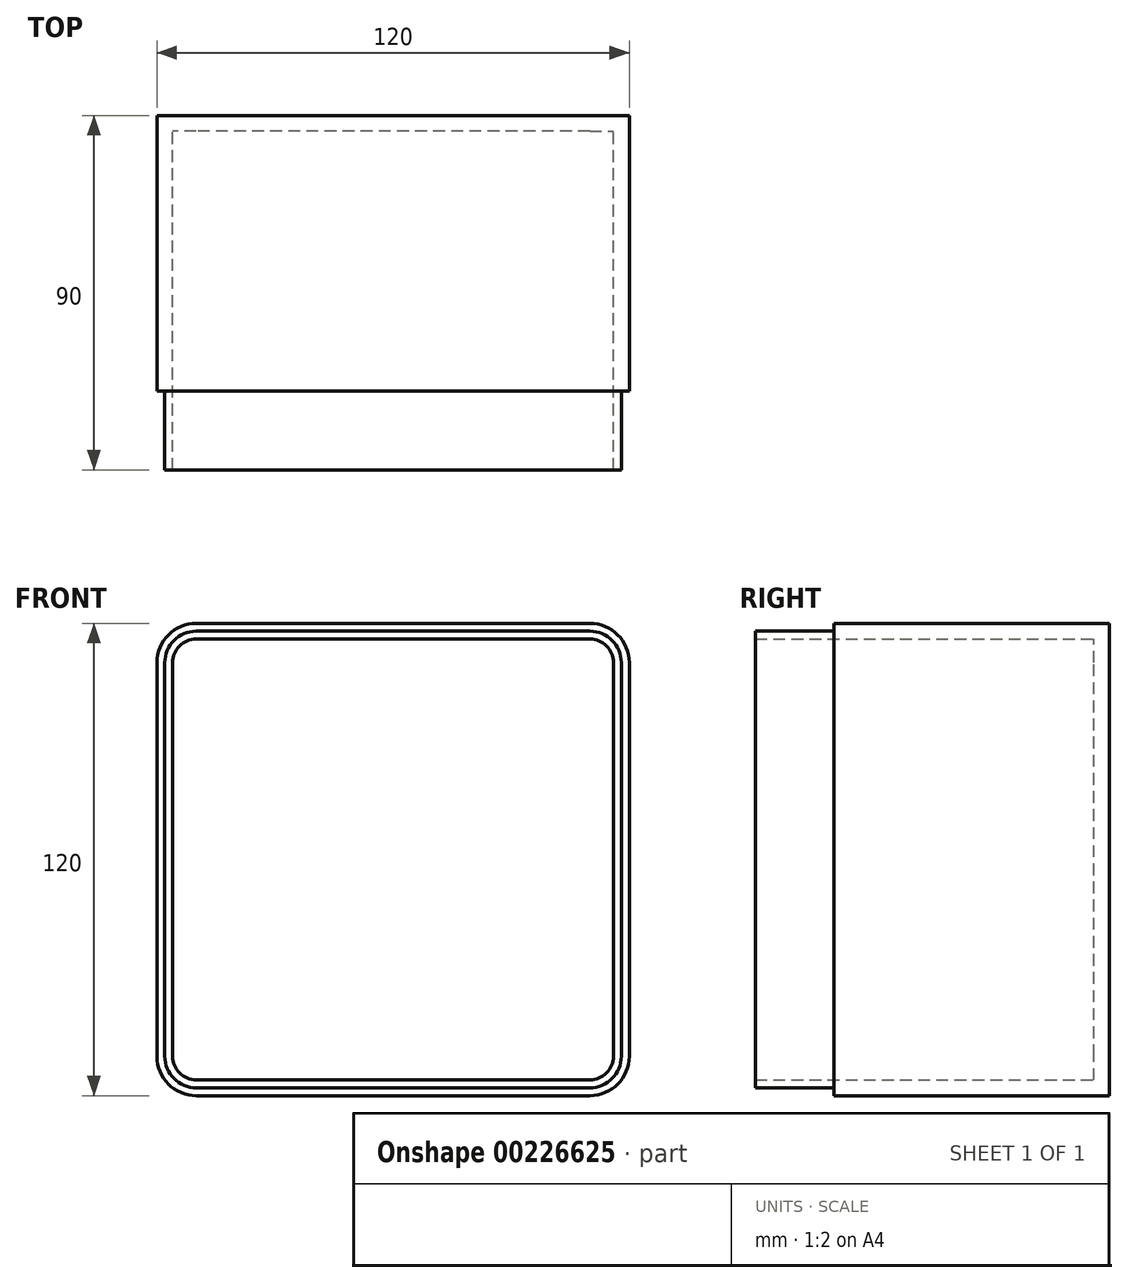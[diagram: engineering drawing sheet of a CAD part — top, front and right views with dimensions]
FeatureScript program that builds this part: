
annotation { "Feature Type Name" : "Feature", "Feature Type Description" : "" }
export const myFeature = defineFeature(function(context is Context, id is Id, definition is map)
    precondition{}
    {
        {
            var Q0;
            Q0=qCreatedBy(makeId("Front.planeOp"),FACE);
            var sketch = newSketch(context, id + "F0", { "sketchPlane" : qUnion([Q0])});
            skLineSegment(sketch, "E0.bottom", {"start": v(0, 0) * mm, "end": v(-120, 0) * mm});
            skLineSegment(sketch, "E0.top", {"start": v(0, 120) * mm, "end": v(-120, 120) * mm});
            skLineSegment(sketch, "E0.left", {"start": v(0, 0) * mm, "end": v(0, 120) * mm});
            skLineSegment(sketch, "E0.right", {"start": v(-120, 0) * mm, "end": v(-120, 120) * mm});
            skSolve(sketch);
        }
        {
            var Q0;
            Q0 = qSketchRegion(id + "F0", true);
            extrude(context, id + "F1", {"entities" : qUnion([Q0]), "depth" : 90 * mm});
        }
        {
            var Q0;
            Q0=makeQuery(id+"F1.opExtrude","SWEPT_EDGE",EDGE,{"disambiguationData":[OSD([sQuery(id+"F0.wireOp",EDGE,"E0.top"),sQuery(id+"F0.wireOp",EDGE,"E0.left")])]});
            var Q1;
            Q1=makeQuery(id+"F1.opExtrude","SWEPT_EDGE",EDGE,{"disambiguationData":[OSD([sQuery(id+"F0.wireOp",EDGE,"E0.top"),sQuery(id+"F0.wireOp",EDGE,"E0.right")])]});
            var Q2;
            Q2=makeQuery(id+"F1.opExtrude","SWEPT_EDGE",EDGE,{"disambiguationData":[OSD([sQuery(id+"F0.wireOp",EDGE,"E0.bottom"),sQuery(id+"F0.wireOp",EDGE,"E0.left")])]});
            var Q3;
            Q3=makeQuery(id+"F1.opExtrude","SWEPT_EDGE",EDGE,{"disambiguationData":[OSD([sQuery(id+"F0.wireOp",EDGE,"E0.bottom"),sQuery(id+"F0.wireOp",EDGE,"E0.right")])]});
            fillet(context, id + "F2", {"entities" : qUnion([Q0, Q1, Q2, Q3]), "radius" : 10 * mm, "tangentPropagation" : true, "allowEdgeOverflow" : false});
        }
        {
            var Q0;
            Q0=makeQuery(id+"F1.opExtrude","CAP_FACE",FACE,{"disambiguationData":[OSD([sQuery(id+"F0.wireOp",EDGE,"E0.bottom"),sQuery(id+"F0.wireOp",EDGE,"E0.top"),sQuery(id+"F0.wireOp",EDGE,"E0.left"),sQuery(id+"F0.wireOp",EDGE,"E0.right")])],"isStart":false});
            shell(context, id + "F3", {"entities" : qUnion([Q0]), "thickness" : 4 * mm});
        }
        {
            var Q0;
            Q0=makeQuery(id+"F1.opExtrude","CAP_FACE",FACE,{"disambiguationData":[OSD([sQuery(id+"F0.wireOp",EDGE,"E0.bottom"),sQuery(id+"F0.wireOp",EDGE,"E0.top"),sQuery(id+"F0.wireOp",EDGE,"E0.left"),sQuery(id+"F0.wireOp",EDGE,"E0.right")])],"isStart":false});
            var sketch = newSketch(context, id + "F4", { "sketchPlane" : qUnion([Q0])});
            skLineSegment(sketch, "E1.0", {"start": v(-120, 10) * mm, "end": v(-120, 110) * mm});
            skArc(sketch, "E2.0", {"start": v(-120, 10) * mm, "mid": v(-117.07, 2.93) * mm, "end": v(-110, 0) * mm});
            skLineSegment(sketch, "E3.0", {"start": v(-10, 0) * mm, "end": v(-110, 0) * mm});
            skArc(sketch, "E4.0", {"start": v(-10, 0) * mm, "mid": v(-2.93, 2.93) * mm, "end": v(0, 10) * mm});
            skLineSegment(sketch, "E5.0", {"start": v(0, 10) * mm, "end": v(0, 110) * mm});
            skArc(sketch, "E6.0", {"start": v(0, 110) * mm, "mid": v(-2.93, 117.07) * mm, "end": v(-10, 120) * mm});
            skLineSegment(sketch, "E7.0", {"start": v(-10, 120) * mm, "end": v(-110, 120) * mm});
            skArc(sketch, "E8.0", {"start": v(-110, 120) * mm, "mid": v(-117.07, 117.07) * mm, "end": v(-120, 110) * mm});
            skArc(sketch, "E9.0", {"start": v(-118, 10) * mm, "mid": v(-115.66, 4.34) * mm, "end": v(-110, 2) * mm});
            skLineSegment(sketch, "E9.1", {"start": v(-10, 2) * mm, "end": v(-110, 2) * mm});
            skLineSegment(sketch, "E9.2", {"start": v(-118, 10) * mm, "end": v(-118, 110) * mm});
            skArc(sketch, "E9.3", {"start": v(-10, 2) * mm, "mid": v(-4.34, 4.34) * mm, "end": v(-2, 10) * mm});
            skArc(sketch, "E9.4", {"start": v(-110, 118) * mm, "mid": v(-115.66, 115.66) * mm, "end": v(-118, 110) * mm});
            skLineSegment(sketch, "E9.5", {"start": v(-10, 118) * mm, "end": v(-110, 118) * mm});
            skArc(sketch, "E9.6", {"start": v(-2, 110) * mm, "mid": v(-4.34, 115.66) * mm, "end": v(-10, 118) * mm});
            skLineSegment(sketch, "E9.7", {"start": v(-2, 10) * mm, "end": v(-2, 110) * mm});
            skSolve(sketch);
        }
        {
            var Q0;
            Q0 = qSketchRegion(id + "F4", true);
            extrude(context, id + "F5", {"entities" : qUnion([Q0]), "operationType" : NewBodyOperationType.REMOVE, "oppositeDirection" : true, "depth" : 20 * mm});
        }
    });
